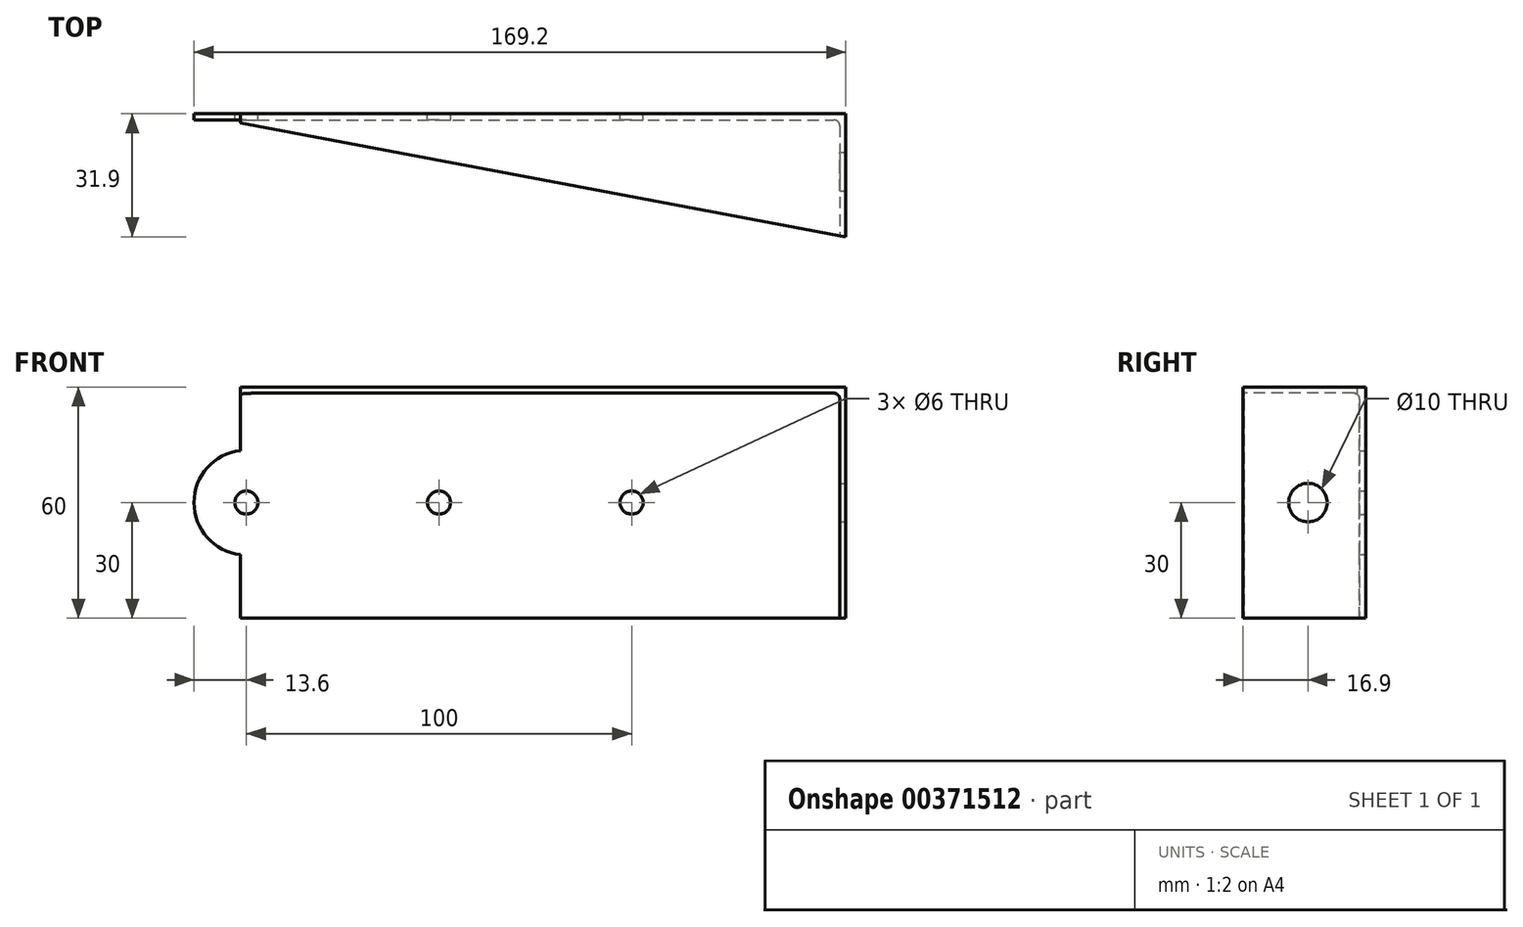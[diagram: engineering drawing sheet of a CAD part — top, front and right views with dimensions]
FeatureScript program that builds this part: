
annotation { "Feature Type Name" : "Feature", "Feature Type Description" : "" }
export const myFeature = defineFeature(function(context is Context, id is Id, definition is map)
    precondition{}
    {
        {
            var Q0;
            Q0=qCreatedBy(makeId("Front.planeOp"),FACE);
            var sketch = newSketch(context, id + "F0", { "sketchPlane" : qUnion([Q0])});
            skLineSegment(sketch, "E0.bottom", {"start": v(-77, 28.4) * mm, "end": v(77, 28.4) * mm});
            skLineSegment(sketch, "E0.top", {"start": v(-77, -28.4) * mm, "end": v(77, -28.4) * mm});
            skLineSegment(sketch, "E0.left", {"start": v(-77, 28.4) * mm, "end": v(-77, 12) * mm});
            skLineSegment(sketch, "E0.right", {"start": v(77, 28.4) * mm, "end": v(77, -28.4) * mm});
            skPoint(sketch, "E0.middle", {"position": v(0, 0) * mm});
            skLineSegment(sketch, "E1", {"start": v(86.5, 0) * mm, "end": v(-99, 0) * mm, "construction": true});
            skArc(sketch, "E2", {"start": v(-77, 12) * mm, "mid": v(-89, 0) * mm, "end": v(-77, -12) * mm});
            skCircle(sketch, "E3", {"center": v(-77, 0) * mm, "radius": 2.12 * mm});
            skLineSegment(sketch, "E4", {"start": v(-27, 6.25) * mm, "end": v(-27, -5.29) * mm, "construction": true});
            skLineSegment(sketch, "E5", {"start": v(23, 4.95) * mm, "end": v(23, -8.23) * mm, "construction": true});
            skLineSegment(sketch, "E6.trimOffspring", {"start": v(-77, -12) * mm, "end": v(-77, -28.4) * mm});
            skLineSegment(sketch, "E7", {"start": v(-77, 12) * mm, "end": v(-77, -12) * mm, "construction": true});
            skSolve(sketch);
        }
        {
            var Q0;
            Q0=makeQuery(id+"F0.imprint","IMPRINT",FACE,{"disambiguationData":[TD([[makeQuery(id+"F0.imprint","IMPRINT",EDGE,{"derivedFrom":sQuery(id+"F0.wireOp",EDGE,"E0.bottom")}),-1.0]])]});
            extrude(context, id + "F1", {"entities" : qUnion([Q0]), "depth" : 30 * mm, "offsetDistance" : 25 * mm});
        }
        {
            var Q0;
            Q0=makeQuery(id+"F1.opExtrude","SWEPT_FACE",FACE,{"disambiguationData":[OSD([sQuery(id+"F0.wireOp",EDGE,"E0.top")])]});
            var sketch = newSketch(context, id + "F2", { "sketchPlane" : qUnion([Q0])});
            skLineSegment(sketch, "E8", {"start": v(77, 30) * mm, "end": v(-77, 1) * mm});
            skLineSegment(sketch, "E9", {"start": v(-77, 1) * mm, "end": v(-89, 1) * mm});
            skLineSegment(sketch, "E10", {"start": v(-89, 1) * mm, "end": v(-89, 30) * mm});
            skLineSegment(sketch, "E11", {"start": v(-89, 30) * mm, "end": v(77, 30) * mm});
            skSolve(sketch);
        }
        {
            var Q0;
            {var subQ0=sQuery(id+"F2.wireOp",EDGE,"E8");Q0=makeQuery(id+"F2.imprint","IMPRINT",FACE,{"disambiguationData":[TD([[makeQuery(id+"F2.imprint","IMPRINT",EDGE,{"derivedFrom":subQ0}),-1.0]])]});}
            var Q1;
            {var subQ0=sQuery(id+"F2.wireOp",EDGE,"E9");Q1=makeQuery(id+"F2.imprint","IMPRINT",FACE,{"disambiguationData":[TD([[makeQuery(id+"F2.imprint","IMPRINT",EDGE,{"derivedFrom":subQ0}),-1.0]])]});}
            extrude(context, id + "F3", {"entities" : qUnion([Q0, Q1]), "operationType" : NewBodyOperationType.REMOVE, "oppositeDirection" : true, "depth" : 62 * mm, "offsetDistance" : 25 * mm});
        }
        {
            var Q0;
            Q0=makeQuery(id+"F3.boolean.opBoolean","COPY",FACE,{"derivedFrom":makeQuery(id+"F3.opExtrude","SWEPT_FACE",FACE,{"disambiguationData":[OSD([sQuery(id+"F2.wireOp",EDGE,"E8")])]})});
            shell(context, id + "F4", {"entities" : qUnion([Q0]), "thickness" : 1.6 * mm, "oppositeDirection" : true});
        }
        {
            var Q0;
            Q0=makeQuery(id+"F1.opExtrude","SWEPT_FACE",FACE,{"disambiguationData":[OSD([sQuery(id+"F0.wireOp",EDGE,"E0.top")])]});
            var sketch = newSketch(context, id + "F5", { "sketchPlane" : qUnion([Q0])});
            skLineSegment(sketch, "E12", {"start": v(77, 0) * mm, "end": v(77, 30) * mm});
            skLineSegment(sketch, "E13", {"start": v(-77.4, 0) * mm, "end": v(77, 0) * mm});
            skLineSegment(sketch, "E14", {"start": v(77, 30) * mm, "end": v(-66.38, 3) * mm});
            skLineSegment(sketch, "E15", {"start": v(-77.4, 0) * mm, "end": v(-91.4, 0) * mm});
            skLineSegment(sketch, "E16", {"start": v(-91.4, 0) * mm, "end": v(-91.4, 3) * mm});
            skLineSegment(sketch, "E17", {"start": v(-91.4, 3) * mm, "end": v(-66.38, 3) * mm});
            skSolve(sketch);
        }
        {
            var Q0;
            Q0=makeQuery(id+"F5.imprint","IMPRINT",FACE,{"disambiguationData":[TD([[makeQuery(id+"F5.imprint","IMPRINT",EDGE,{"derivedFrom":sQuery(id+"F5.wireOp",EDGE,"E12")}),1.0]])]});
            var Q1;
            {var subQ4=sQuery(id+"F5.wireOp",EDGE,"E15");Q1=makeQuery(id+"F5.imprint","IMPRINT",FACE,{"disambiguationData":[TD([[makeQuery(id+"F5.imprint","IMPRINT",EDGE,{"derivedFrom":subQ4}),-1.0]])]});}
            extrude(context, id + "F6", {"entities" : qUnion([Q0, Q1]), "operationType" : NewBodyOperationType.REMOVE, "oppositeDirection" : true, "depth" : 58.4 * mm, "offsetDistance" : 25 * mm});
        }
        {
            var Q0;
            Q0=makeQuery(id+"F1.opExtrude","CAP_FACE",FACE,{"disambiguationData":[OSD([sQuery(id+"F0.wireOp",EDGE,"E0.bottom"),sQuery(id+"F0.wireOp",EDGE,"E0.top"),sQuery(id+"F0.wireOp",EDGE,"E0.left"),sQuery(id+"F0.wireOp",EDGE,"E0.right"),sQuery(id+"F0.wireOp",EDGE,"E2"),sQuery(id+"F0.wireOp",EDGE,"E3"),sQuery(id+"F0.wireOp",EDGE,"E6.trimOffspring")])],"isStart":true});
            var sketch = newSketch(context, id + "F7", { "sketchPlane" : qUnion([Q0])});
            skCircle(sketch, "E18", {"center": v(27, 0) * mm, "radius": 3 * mm});
            skCircle(sketch, "E19", {"center": v(-23, 0) * mm, "radius": 3 * mm});
            skCircle(sketch, "E20", {"center": v(77, 0) * mm, "radius": 3 * mm});
            skSolve(sketch);
        }
        {
            var Q0;
            Q0=makeQuery(id+"F7.imprint","IMPRINT",FACE,{"disambiguationData":[TD([[makeQuery(id+"F7.imprint","IMPRINT",EDGE,{"derivedFrom":sQuery(id+"F7.wireOp",EDGE,"E20")}),1.0]])]});
            var Q1;
            Q1=makeQuery(id+"F7.imprint","IMPRINT",FACE,{"disambiguationData":[TD([[makeQuery(id+"F7.imprint","IMPRINT",EDGE,{"derivedFrom":sQuery(id+"F7.wireOp",EDGE,"E18")}),1.0]])]});
            var Q2;
            Q2=makeQuery(id+"F7.imprint","IMPRINT",FACE,{"disambiguationData":[TD([[makeQuery(id+"F7.imprint","IMPRINT",EDGE,{"derivedFrom":sQuery(id+"F7.wireOp",EDGE,"E19")}),1.0]])]});
            extrude(context, id + "F8", {"entities" : qUnion([Q0, Q1, Q2]), "operationType" : NewBodyOperationType.REMOVE, "oppositeDirection" : true, "depth" : 25 * mm, "offsetDistance" : 25 * mm});
        }
        {
            var Q0;
            Q0=makeQuery(id+"F1.opExtrude","SWEPT_FACE",FACE,{"disambiguationData":[OSD([sQuery(id+"F0.wireOp",EDGE,"E0.right")])]});
            var sketch = newSketch(context, id + "F9", { "sketchPlane" : qUnion([Q0])});
            skCircle(sketch, "E21", {"center": v(-13.4, 0) * mm, "radius": 5 * mm});
            skSolve(sketch);
        }
        {
            var Q0;
            Q0=makeQuery(id+"F9.imprint","IMPRINT",FACE,{"disambiguationData":[TD([[makeQuery(id+"F9.imprint","IMPRINT",EDGE,{"derivedFrom":sQuery(id+"F9.wireOp",EDGE,"E21")}),1.0]])]});
            extrude(context, id + "F10", {"entities" : qUnion([Q0]), "operationType" : NewBodyOperationType.REMOVE, "oppositeDirection" : true, "depth" : 3 * mm, "offsetDistance" : 25 * mm});
        }
        {
            var Q0;
            Q0=makeQuery(id+"F6.boolean.opBoolean","MERGE",EDGE,{"derivedFrom":[makeQuery(id+"F4.opShell","OFFSET_EDGE",EDGE,{"disambiguationData":[OSD([sQuery(id+"F0.wireOp",EDGE,"E0.bottom")])]})],"fromTools":[makeQuery(id+"F6.opExtrude","CAP_EDGE",EDGE,{"disambiguationData":[OSD([sQuery(id+"F5.wireOp",EDGE,"E13"),sQuery(id+"F5.wireOp",EDGE,"E15")])],"isStart":false})]});
            var Q1;
            Q1=makeQuery(id+"F4.opShell","OFFSET_EDGE",EDGE,{"disambiguationData":[OSD([sQuery(id+"F0.wireOp",EDGE,"E0.bottom"),sQuery(id+"F0.wireOp",EDGE,"E0.right")])]});
            var Q2;
            Q2=makeQuery(id+"F6.boolean.opBoolean","MERGE",EDGE,{"derivedFrom":[makeQuery(id+"F4.opShell","OFFSET_EDGE",EDGE,{"disambiguationData":[OSD([sQuery(id+"F0.wireOp",EDGE,"E0.right")])]})],"fromTools":[makeQuery(id+"F6.opExtrude","SWEPT_EDGE",EDGE,{"disambiguationData":[OSD([sQuery(id+"F5.wireOp",EDGE,"E12"),sQuery(id+"F5.wireOp",EDGE,"E13")])]})]});
            fillet(context, id + "F11", {"entities" : qUnion([Q0, Q1, Q2]), "tangentPropagation" : true, "radius" : 1.5 * mm, "defaultsChanged" : false, "vertexSettings" : [], "allowEdgeOverflow" : false});
        }
    });
